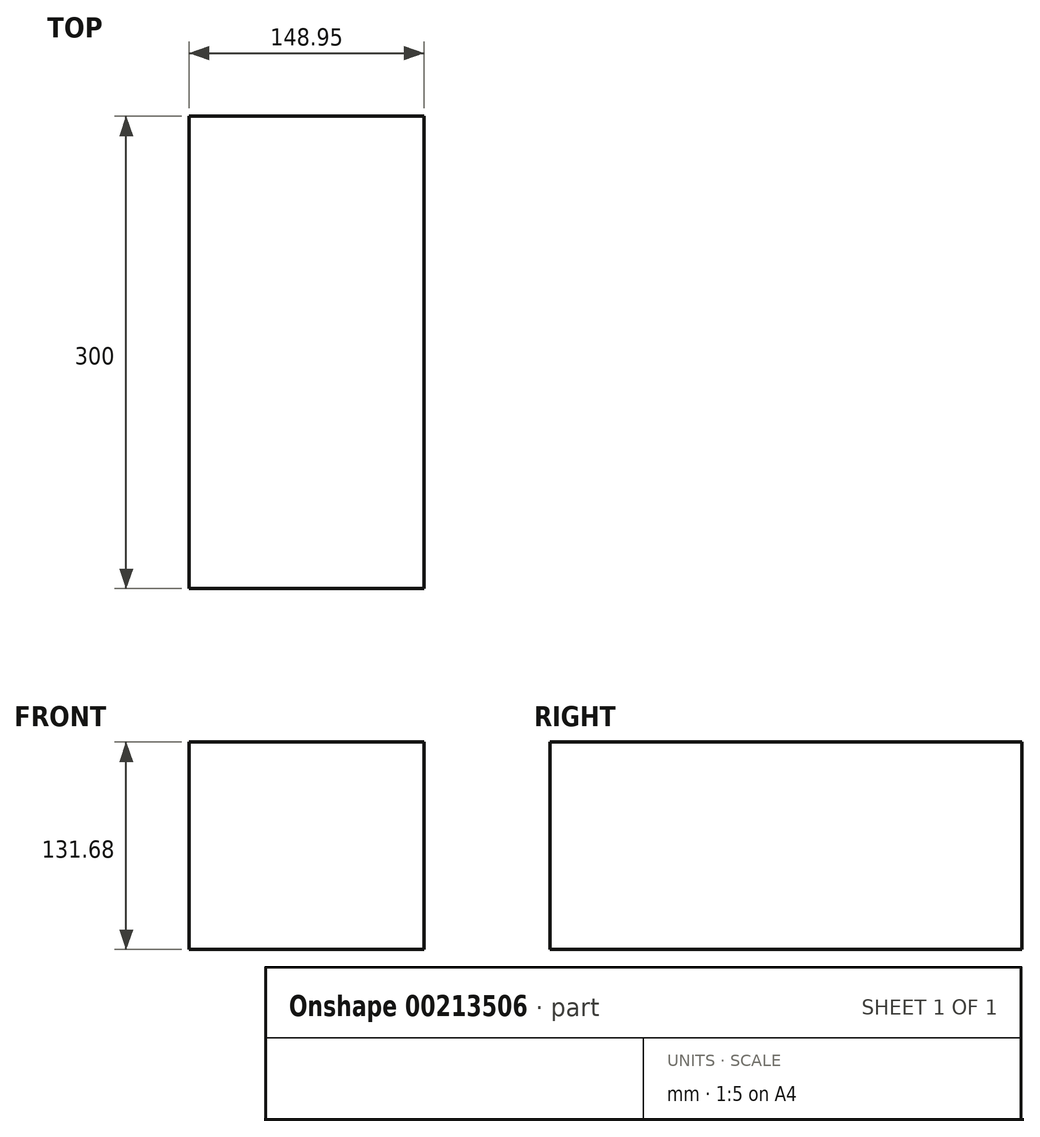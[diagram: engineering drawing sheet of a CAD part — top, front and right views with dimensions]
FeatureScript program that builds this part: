
annotation { "Feature Type Name" : "Feature", "Feature Type Description" : "" }
export const myFeature = defineFeature(function(context is Context, id is Id, definition is map)
    precondition{}
    {
        {
            var Q0;
            Q0=qCreatedBy(makeId("Front.planeOp"),FACE);
            var sketch = newSketch(context, id + "F0", { "sketchPlane" : qUnion([Q0])});
            skLineSegment(sketch, "E0.bottom", {"start": v(-68.87, 61.65) * mm, "end": v(80.08, 61.65) * mm});
            skLineSegment(sketch, "E0.top", {"start": v(-68.87, -70.03) * mm, "end": v(80.08, -70.03) * mm});
            skLineSegment(sketch, "E0.left", {"start": v(-68.87, 61.65) * mm, "end": v(-68.87, -70.03) * mm});
            skLineSegment(sketch, "E0.right", {"start": v(80.08, 61.65) * mm, "end": v(80.08, -70.03) * mm});
            skSolve(sketch);
        }
        {
            var Q0;
            Q0=makeQuery(id+"F0.imprint","IMPRINT",FACE,{"disambiguationData":[TD([[makeQuery(id+"F0.imprint","IMPRINT",EDGE,{"derivedFrom":sQuery(id+"F0.wireOp",EDGE,"E0.bottom")}),-1.0]])]});
            extrude(context, id + "F1", {"entities" : qUnion([Q0]), "endBound" : BoundingType.SYMMETRIC, "oppositeDirection" : true, "depth" : 300 * mm});
        }
    });
